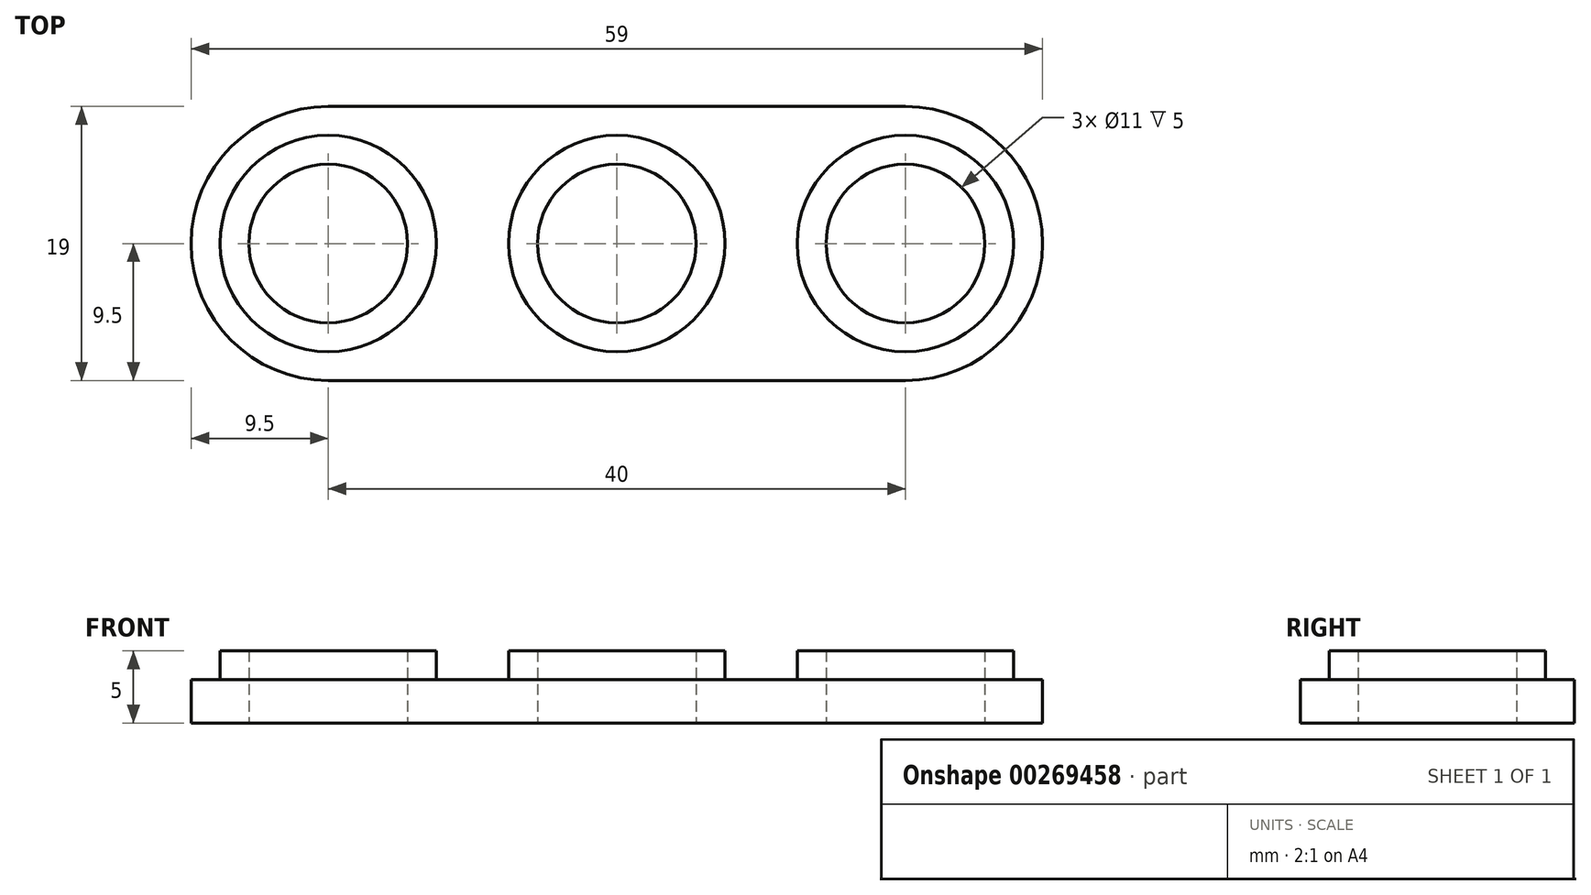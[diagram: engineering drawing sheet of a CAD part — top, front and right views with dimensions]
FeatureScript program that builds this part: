
annotation { "Feature Type Name" : "Feature", "Feature Type Description" : "" }
export const myFeature = defineFeature(function(context is Context, id is Id, definition is map)
    precondition{}
    {
        {
            assignVariable(context, id + "F0", {"name" : "e", "anyValue" : 3});
        }
        {
            assignVariable(context, id + "F1", {"name" : "h0", "anyValue" : 2});
        }
        {
            var Q0;
            Q0=qCreatedBy(makeId("Top.planeOp"),FACE);
            var sketch = newSketch(context, id + "F2", { "sketchPlane" : qUnion([Q0])});
            skLineSegment(sketch, "E0.bottom", {"start": v(0, 9.5) * mm, "end": v(40, 9.5) * mm});
            skLineSegment(sketch, "E0.top", {"start": v(0, -9.5) * mm, "end": v(40, -9.5) * mm});
            skLineSegment(sketch, "E0.left", {"start": v(-9.5, 0) * mm, "end": v(-9.5, 0) * mm});
            skLineSegment(sketch, "E0.right", {"start": v(49.5, 0) * mm, "end": v(49.5, 0) * mm});
            skPoint(sketch, "E1", {"position": v(-9.5, 0) * mm});
            skCircle(sketch, "E2", {"center": v(0, 0) * mm, "radius": 5.5 * mm});
            skPoint(sketch, "E3.visualSharp", {"position": v(49.5, 9.5) * mm});
            skArc(sketch, "E3.filletArc", {"start": v(49.5, 0) * mm, "mid": v(46.72, 6.72) * mm, "end": v(40, 9.5) * mm});
            skPoint(sketch, "E4.visualSharp", {"position": v(49.5, -9.5) * mm});
            skArc(sketch, "E4.filletArc", {"start": v(40, -9.5) * mm, "mid": v(46.72, -6.72) * mm, "end": v(49.5, 0) * mm});
            skPoint(sketch, "E5.visualSharp", {"position": v(-9.5, -9.5) * mm});
            skArc(sketch, "E5.filletArc", {"start": v(-9.5, 0) * mm, "mid": v(-6.72, -6.72) * mm, "end": v(0, -9.5) * mm});
            skPoint(sketch, "E6.visualSharp", {"position": v(-9.5, 9.5) * mm});
            skArc(sketch, "E6.filletArc", {"start": v(0, 9.5) * mm, "mid": v(-6.72, 6.72) * mm, "end": v(-9.5, 0) * mm});
            skCircle(sketch, "E7", {"center": v(0, 0) * mm, "radius": 7.5 * mm});
            skCircle(sketch, "E8.1.0.0", {"center": v(20, 0) * mm, "radius": 5.5 * mm});
            skCircle(sketch, "E8.1.0.1", {"center": v(20, 0) * mm, "radius": 7.5 * mm});
            skCircle(sketch, "E8.2.0.0", {"center": v(40, 0) * mm, "radius": 5.5 * mm});
            skCircle(sketch, "E8.2.0.1", {"center": v(40, 0) * mm, "radius": 7.5 * mm});
            skLineSegment(sketch, "E8.direction1", {"start": v(0, 0) * mm, "end": v(20, 0) * mm, "construction": true});
            skSolve(sketch);
        }
        {
            var Q0;
            Q0=qSketchRegion(id+"F2",true);
            extrude(context, id + "F3", {"entities" : qUnion([Q0]), "depth" : (getVariable(context, 'e')) * mm});
        }
        {
            var Q0;
            Q0=makeQuery(id+"F2.imprint","IMPRINT",FACE,{"disambiguationData":[TD([[makeQuery(id+"F2.imprint","IMPRINT",EDGE,{"derivedFrom":sQuery(id+"F2.wireOp",EDGE,"E2")}),-1.0]])]});
            var Q1;
            Q1=makeQuery(id+"F2.imprint","IMPRINT",FACE,{"disambiguationData":[TD([[makeQuery(id+"F2.imprint","IMPRINT",EDGE,{"derivedFrom":sQuery(id+"F2.wireOp",EDGE,"E8.1.0.0")}),-1.0]])]});
            var Q2;
            Q2=makeQuery(id+"F2.imprint","IMPRINT",FACE,{"disambiguationData":[TD([[makeQuery(id+"F2.imprint","IMPRINT",EDGE,{"derivedFrom":sQuery(id+"F2.wireOp",EDGE,"E8.2.0.0")}),-1.0]])]});
            var Q3;
            Q3=makeQuery(id+"F2.imprint","IMPRINT",FACE,{"disambiguationData":[TD([[makeQuery(id+"F2.imprint","IMPRINT",EDGE,{"derivedFrom":sQuery(id+"F2.wireOp",EDGE,"E8.3.0.0")}),-1.0]])]});
            var Q4;
            Q4=makeQuery(id+"F2.imprint","IMPRINT",FACE,{"disambiguationData":[TD([[makeQuery(id+"F2.imprint","IMPRINT",EDGE,{"derivedFrom":sQuery(id+"F2.wireOp",EDGE,"E8.4.0.0")}),-1.0]])]});
            var Q5;
            Q5=makeQuery(id+"F2.imprint","IMPRINT",FACE,{"disambiguationData":[TD([[makeQuery(id+"F2.imprint","IMPRINT",EDGE,{"derivedFrom":sQuery(id+"F2.wireOp",EDGE,"4ce812f6-2cef-4762-a406-8d516c31bb4a.0.3.0")}),-1.0]])]});
            extrude(context, id + "F4", {"entities" : qUnion([Q0, Q1, Q2, Q3, Q4, Q5]), "operationType" : NewBodyOperationType.ADD, "depth" : (getVariable(context, 'e') + getVariable(context, 'h0')) * mm});
        }
    });
